# Revit family: Gira_510300
name_source: partatom
category: Allgemeines Modell
revit_build: Autodesk Revit 2017 (Build: 20160225_1515(x64)
units: mm (PartAtom-declared; Revit-internal decimal feet)

## family parameters
Basisbauteil = Fläche
Beim Laden mit Abzugskörper schneiden = Nein
Bemaßung runder Anschluss = Durchmesser verwenden
Gemeinsam genutzt = Nein
Kann Basisbauteil für Bewehrung sein = Nein
Raumberechnungspunkt = Nein
Teiletyp = Normal

## types (1)
- RF Tastsens. 3f KNX
    Andere Bussysteme = ohne
    Anzahl der Betätigungspunkte = 6
    Anzahl der Tasten = 3
    Ausführung der Oberfläche = nicht zutreffend
    BIM = https://media.stage.bim.site
    BIMSITE_PRODUCT_ID = c2e1978726a777219db44485629d34b0aefbabc7
    Beschreibung = KNX RF Tastsensor 3fach System 55 Inbetriebnahme-Wippe Die KNX RF Tastsensoren senden bei Tastenbetätigung in Abhängigkeit der Parametereinstellung bei geladenem Applikationsprogramm drahtlos KNX Telegramme aus. Dies können bspw. Telegramme zum Schalten oder Tasten, zum Dimmen oder zur Jalousiesteuerung sein. Auch ist es möglich, Wertgeberfunktionen zu programmieren (Dimmwertgeber und Szenennebenstellen).  Merkmale:  Bestätigungsfunktion sowie Sende- und Statusanzeige über 2-farbige LED (rot grün) separat für jede Taste durch 2-stufige Anzeigefunktion.  Statusanzeige optional über separate 1-Bit-Status-Kommunikationsobjekte.  Sende- und Bestätigungsanzeige abschaltbar.  Auf Wänden kann der Tastsensor mittels Schrauben befestigt bzw. auf glatten oder transparenten Oberflächen mit einer Montageplatte aufgeklebt werden.  Projektierung, Inbetriebnahme und Parametrierung erfolgen über ETS (Version 5 oder neuer).  Batteriebetriebenes Gerät. Funktion Schalten":  Wippen- oder Tastenfunktion.  Befehl beim Drücken und beim Loslassen parametrierbar (EIN, AUS, UM, keine Reaktion). Funktion "Dimmen":  Wippenfunktion.  Befehl beim Drücken der Wippe (rechte und linke Taste) parametrierbar (heller - EIN, dunkler - AUS). Funktion "Jalousie":  Wippenfunktion.  Befehl beim Drücken der Wippe (rechte und linke Taste) parametrierbar (AUF, AB, UM).  Zeit zwischen Kurz- und Langzeitbefehl parametrierbar. Funktionen "Wertgeber" und "Szenennebenstelle":  Wippenfunktion.  Befehl beim Drücken der Wippe (rechte und linke Taste) parametrierbar (Werte 0 bis 255, 0 bis 100% oder Szenennummer).  Bei Szenennebenstelle: Speicherfunktion möglich.  Hinweise :  Batterien sind Verbrauchsgüter und müssen regelmäßig ersetzt werden. Bitte beachten Sie die Vorschriften zur Entsorgung von gebrauchten Batterien.  Der Tastsensor wird mit einer programmneutralen Inbetriebnahme-Wippe geliefert. Das passende Wippenset zum Schalterprogramm ist separat zu bestellen.  Bei Verwendung von Wippensets und oder Abdeckrahmen kann es zu Reichweiteneinbußen kommen."
    Bussystem Funkbus = Nein
    Bussystem KNX = Ja
    Bussystem KNX-Funk = Ja
    Bussystem LON = Nein
    Bussystem Powernet = Nein
    Datenblatt = https://media.stage.bim.site
    Datenblatt 1 = https://media.stage.bim.site
    Farbe = sonstige
    GTIN = 4010337017257
    HAN = 510300
    HeinzeBIM = https://www.heinze.de
    Hersteller = Gira
    Kosten = 0 $
    Mit Beschriftungsfeld = Nein
    Mit Busankopplung = Nein
    Mit Diebstahl-/Demontageschutz = Nein
    Mit Display = Nein
    Mit Infrarotsensor = Nein
    Mit LED-Anzeige = Ja
    Mit Raumthermostat = Nein
    Montageart = Unterputz
    Oberfläche Text = sonstige
    Produktseite = https://media.stage.bim.site
    Schutzart (IP) = IP20
    Transparent = Nein
    Typname = RF Tastsens. 3f KNX
    URL = https://www.gira.de
    Vorgabe-Ansicht = 1219 mm
    Werkstoff Text = sonstige
    Werkstoffgüte = sonstige

## geometry (parser evidence)
native form markers: Sweep x2
no freeform markers — native parametric forms only
